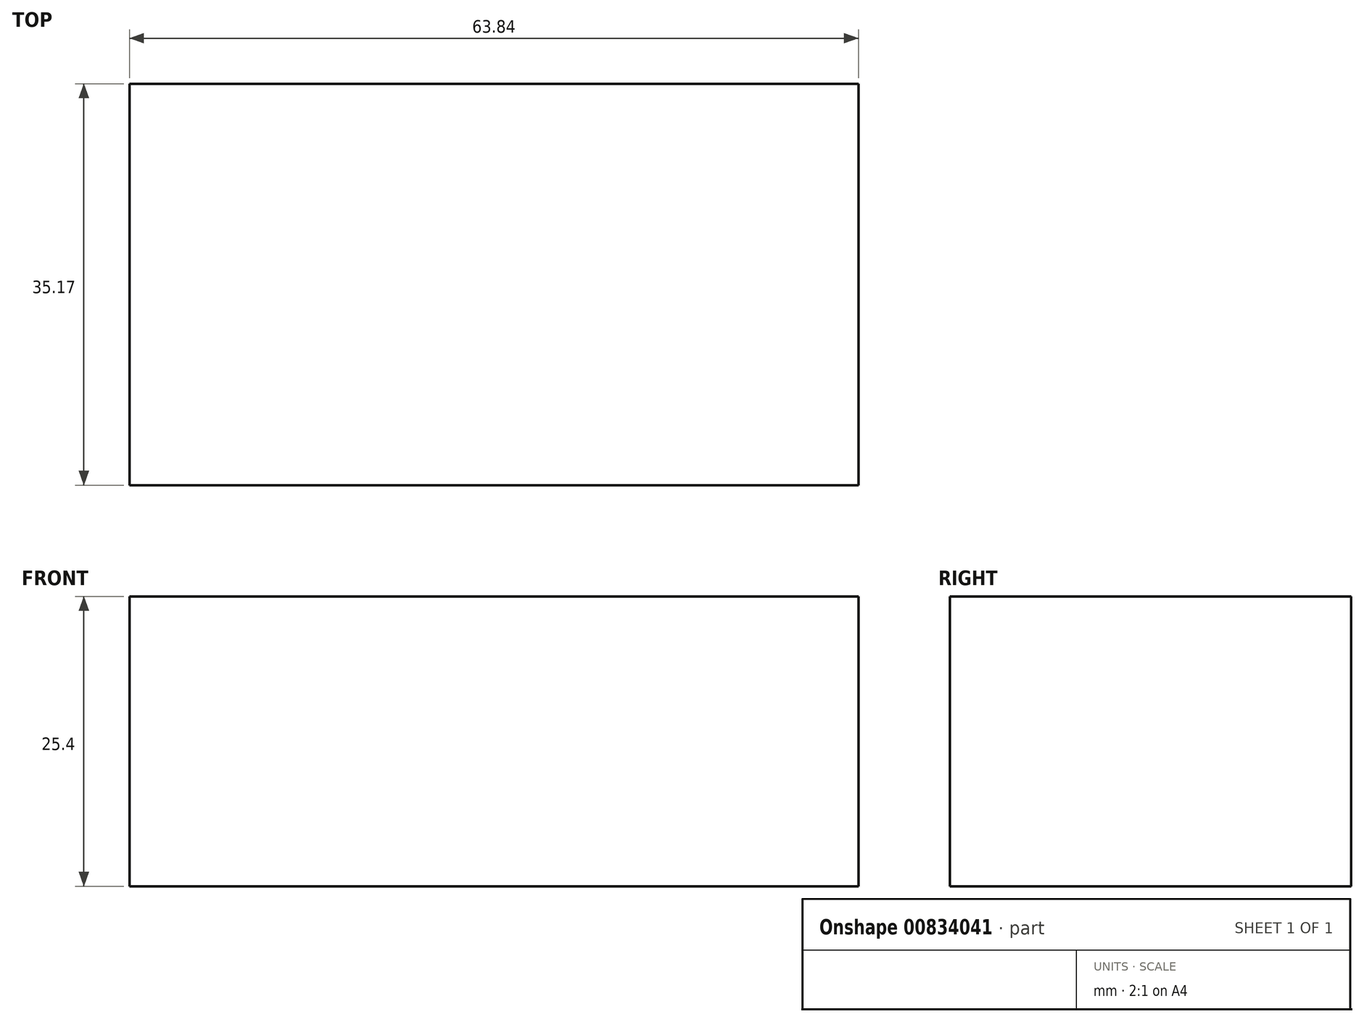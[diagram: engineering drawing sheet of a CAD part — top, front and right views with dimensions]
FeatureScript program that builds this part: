
annotation { "Feature Type Name" : "Feature", "Feature Type Description" : "" }
export const myFeature = defineFeature(function(context is Context, id is Id, definition is map)
    precondition{}
    {
        {
            var Q0;
            Q0=qCreatedBy(makeId("Top.planeOp"),FACE);
            var sketch = newSketch(context, id + "F0", { "sketchPlane" : qUnion([Q0])});
            skLineSegment(sketch, "E0.bottom", {"start": v(0, 0) * mm, "end": v(63.84, 0) * mm});
            skLineSegment(sketch, "E0.top", {"start": v(0, 35.17) * mm, "end": v(63.84, 35.17) * mm});
            skLineSegment(sketch, "E0.left", {"start": v(0, 0) * mm, "end": v(0, 35.17) * mm});
            skLineSegment(sketch, "E0.right", {"start": v(63.84, 0) * mm, "end": v(63.84, 35.17) * mm});
            skLineSegment(sketch, "E1.bottom", {"start": v(22.75, 82.07) * mm, "end": v(-40.95, 82.07) * mm});
            skLineSegment(sketch, "E1.top", {"start": v(22.75, 15.26) * mm, "end": v(-40.95, 15.26) * mm});
            skLineSegment(sketch, "E1.left", {"start": v(22.75, 82.07) * mm, "end": v(22.75, 15.26) * mm});
            skLineSegment(sketch, "E1.right", {"start": v(-40.95, 82.07) * mm, "end": v(-40.95, 15.26) * mm});
            skSolve(sketch);
        }
        {
            var Q0;
            {var subQ1=sQuery(id+"F0.wireOp",EDGE,"E0.bottom");Q0=makeQuery(id+"F0.imprint","IMPRINT",FACE,{"disambiguationData":[TD([[makeQuery(id+"F0.imprint","IMPRINT",EDGE,{"derivedFrom":subQ1}),1.0]])]});}
            var Q1;
            {var subQ0=sQuery(id+"F0.wireOp",EDGE,"E0.left");var subQ1=sQuery(id+"F0.wireOp",EDGE,"E0.top");var subQ2=makeQuery(id+"F0.imprint","INTERSECT",VERTEX,{"derivedFrom":[subQ1,subQ0]});Q1=makeQuery(id+"F0.imprint","IMPRINT",FACE,{"disambiguationData":[TD([[makeQuery(id+"F0.imprint","IMPRINT",EDGE,{"disambiguationData":[TD([[subQ2,-1.0]])],"derivedFrom":subQ1}),-1.0]])]});}
            extrude(context, id + "F1", {"entities" : qUnion([Q0, Q1]), "endBound" : BoundingType.SYMMETRIC, "depth" : 25.4 * mm, "offsetDistance" : 25.4 * mm});
        }
    });
